# Revit family: LBTYP009
name_source: partatom
category: Furniture
units: mm (PartAtom-declared; Revit-internal decimal feet)

## family parameters
Always vertical = Yes
Cut with Voids When Loaded = No
OmniClass Number = 23.40.20.00
OmniClass Title = General Furniture and Specialties
Render Appearance Source = Family Geometry
Room Calculation Point = No
Shared = No
Work Plane-Based = No

## types (1)
- LBTYP009
    Cost = 53167 $
    Default Elevation = 0 mm  [stored 0 ft]
    Description = 13 x Rutland Perch Chair Height Adjustable - Configurable, 2 x CB Community EP Mid Mount 18d x 58h x 21h, 4 x CB Community Single Height Hidden Box Drawers 13H x 36W x 18, 2 x CB Community Spine No Pwr 36w x 18d, 1 x CB Community Spine Pwr 1 Side 72w x 18d, 1 x CB Community Spine Hutch S 72w x18d x 36h, 2 x CB Community Spine Hutch K 36w x 18d x 37h, 2 x LB LOUNGE LEDGE KIT 13"d X 48"w, 1 x LB LOUNGE LEDGE KIT 13"d X 60"w, 3 x LB LOUNGE LEDGE KIT 13"d X 66"w, 2 x LB LOUNGE, CORNER, 42 TALL, SOLID BASE, REAR OVERLAY, LEFT, 1 x LB Lounge 3 Seat 42H X 66W X 30 Open Base, 2 x LB Lounge 3 Seat 42H X 72W X 30 Open Base, 1 x TBL, PBL, KNF, 36Dx16H, DISC, GLD
    Exported From CET Designer = Yes
    Manufacturer = AIS
    Model = 6470C
    Show LBTYP009 = Yes
    VisibilityIndex = 0

note: [stored X ft] marks values corroborated as IEEE doubles in the binary element streams (Revit-internal decimal feet)

## geometry (parser evidence)
native form markers: Sweep x2
no freeform markers — native parametric forms only
